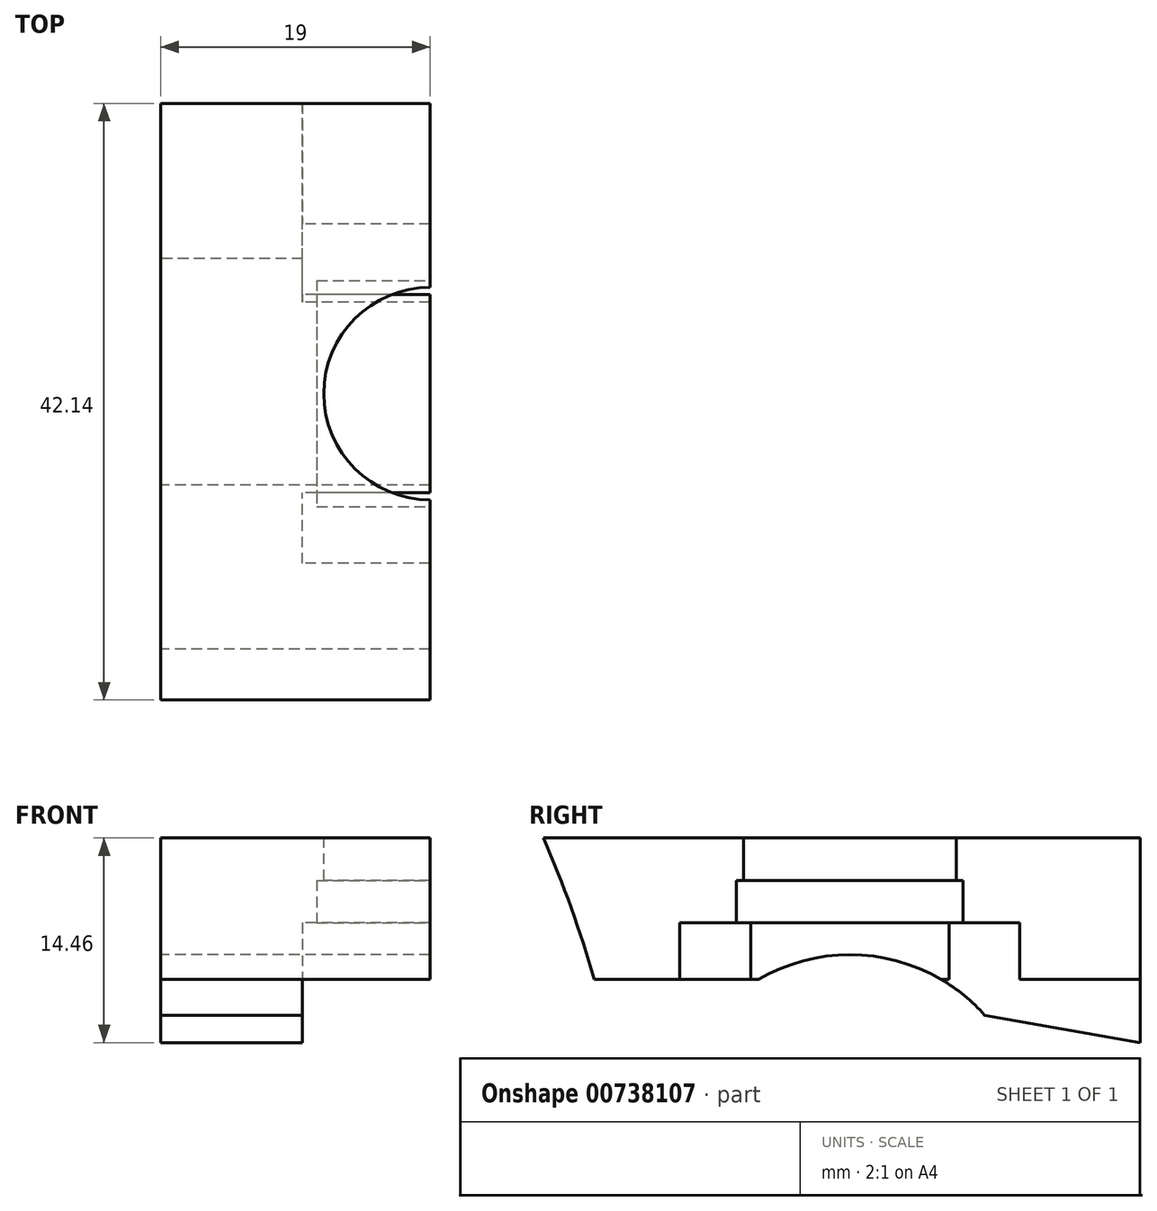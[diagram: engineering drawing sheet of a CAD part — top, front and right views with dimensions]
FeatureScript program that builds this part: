
annotation { "Feature Type Name" : "Feature", "Feature Type Description" : "" }
export const myFeature = defineFeature(function(context is Context, id is Id, definition is map)
    precondition{}
    {
        {
            var Q0;
            Q0=qCreatedBy(makeId("Right.planeOp"),FACE);
            var sketch = newSketch(context, id + "F0", { "sketchPlane" : qUnion([Q0])});
            skLineSegment(sketch, "E0.bottom", {"start": v(21.65, -4.52) * mm, "end": v(-0.35, -4.52) * mm});
            skLineSegment(sketch, "E0.top", {"start": v(21.65, -14.52) * mm, "end": v(-0.35, -14.52) * mm});
            skLineSegment(sketch, "E0.left", {"start": v(21.65, -4.52) * mm, "end": v(21.65, -14.52) * mm});
            skLineSegment(sketch, "E0.right", {"start": v(-0.35, -4.52) * mm, "end": v(-0.35, -14.52) * mm});
            skSolve(sketch);
        }
        {
            var Q0;
            Q0=makeQuery(id+"F0.imprint","IMPRINT",FACE,{"disambiguationData":[TD([[makeQuery(id+"F0.imprint","IMPRINT",EDGE,{"derivedFrom":sQuery(id+"F0.wireOp",EDGE,"E0.bottom")}),1.0]])]});
            extrude(context, id + "F1", {"entities" : qUnion([Q0]), "depth" : 19 * mm, "offsetDistance" : 25 * mm});
        }
        {
            var Q0;
            Q0=makeQuery(id+"FDOM7TivN4VhnVm_1.boolean.opBoolean","MERGE",FACE,{"derivedFrom":[makeQuery(id+"F1.opExtrude","SWEPT_FACE",FACE,{"disambiguationData":[OSD([sQuery(id+"F0.wireOp",EDGE,"E0.bottom")])]}),makeQuery(id+"FDOM7TivN4VhnVm_1.opExtrude","CAP_FACE",FACE,{"disambiguationData":[OSD([sQuery(id+"F9GzfwsNW7Oczpo_1.wireOp",EDGE,"jp0AWD4a-2oyx-ba6K-arvr-44EEn8cdPX9W"),sQuery(id+"F9GzfwsNW7Oczpo_1.wireOp",EDGE,"fE45tPoF-SBnd-VzeE-5eZE-0BWyOUgTPYKQ.bottom"),sQuery(id+"F9GzfwsNW7Oczpo_1.wireOp",EDGE,"fE45tPoF-SBnd-VzeE-5eZE-0BWyOUgTPYKQ.top"),sQuery(id+"F9GzfwsNW7Oczpo_1.wireOp",EDGE,"fE45tPoF-SBnd-VzeE-5eZE-0BWyOUgTPYKQ.left"),sQuery(id+"F9GzfwsNW7Oczpo_1.wireOp",EDGE,"fE45tPoF-SBnd-VzeE-5eZE-0BWyOUgTPYKQ.right")])],"isStart":true})]});
            var sketch = newSketch(context, id + "F2", { "sketchPlane" : qUnion([Q0])});
            skLineSegment(sketch, "E1.bottom", {"start": v(19, -0.35) * mm, "end": v(0, -0.35) * mm});
            skLineSegment(sketch, "E1.top", {"start": v(19, -19.35) * mm, "end": v(0, -19.35) * mm});
            skLineSegment(sketch, "E1.left", {"start": v(19, -0.35) * mm, "end": v(19, -19.35) * mm});
            skLineSegment(sketch, "E1.right", {"start": v(0, -0.35) * mm, "end": v(0, -19.35) * mm});
            skSolve(sketch);
        }
        {
            var Q0;
            {var subQ0=sQuery(id+"F2.wireOp",EDGE,"KGAb659G-aQRa-flcd-oOIB-gSZ9gIRepCPd.top");Q0=makeQuery(id+"F2.imprint","IMPRINT",FACE,{"disambiguationData":[TD([[makeQuery(id+"F2.imprint","IMPRINT",EDGE,{"derivedFrom":subQ0}),-1.0]])]});}
            var Q1;
            Q1=makeQuery(id+"F2.imprint","IMPRINT",FACE,{"disambiguationData":[TD([[makeQuery(id+"F2.imprint","IMPRINT",EDGE,{"derivedFrom":sQuery(id+"F2.wireOp",EDGE,"E1.bottom")}),1.0]])]});
            extrude(context, id + "F3", {"entities" : qUnion([Q0, Q1]), "operationType" : NewBodyOperationType.ADD, "depth" : -10 * mm, "offsetDistance" : 25 * mm});
        }
        {
            var Q0;
            Q0=makeQuery(id+"F3.boolean.opBoolean","MERGE",FACE,{"derivedFrom":[makeQuery(id+"F1.opExtrude","SWEPT_FACE",FACE,{"disambiguationData":[OSD([sQuery(id+"F0.wireOp",EDGE,"E0.top")])]}),makeQuery(id+"F3.opExtrude","CAP_FACE",FACE,{"disambiguationData":[OSD([sQuery(id+"F0.wireOp",EDGE,"E0.bottom"),sQuery(id+"F0.wireOp",EDGE,"E0.right"),sQuery(id+"F2.wireOp",EDGE,"KGAb659G-aQRa-flcd-oOIB-gSZ9gIRepCPd.top"),sQuery(id+"F2.wireOp",EDGE,"KGAb659G-aQRa-flcd-oOIB-gSZ9gIRepCPd.left"),sQuery(id+"F2.wireOp",EDGE,"KGAb659G-aQRa-flcd-oOIB-gSZ9gIRepCPd.right")])],"isStart":false})]});
            var sketch = newSketch(context, id + "F4", { "sketchPlane" : qUnion([Q0])});
            skLineSegment(sketch, "E2.bottom", {"start": v(19, 10.85) * mm, "end": v(10, 10.85) * mm});
            skLineSegment(sketch, "E2.top", {"start": v(19, 5.85) * mm, "end": v(10, 5.85) * mm});
            skLineSegment(sketch, "E2.left", {"start": v(19, 10.85) * mm, "end": v(19, 5.85) * mm});
            skLineSegment(sketch, "E2.right", {"start": v(10, 10.85) * mm, "end": v(10, 5.85) * mm});
            skLineSegment(sketch, "E3.bottom", {"start": v(19, -8.15) * mm, "end": v(10, -8.15) * mm});
            skLineSegment(sketch, "E3.top", {"start": v(19, -13.15) * mm, "end": v(10, -13.15) * mm});
            skLineSegment(sketch, "E3.left", {"start": v(19, -8.15) * mm, "end": v(19, -13.15) * mm});
            skLineSegment(sketch, "E3.right", {"start": v(10, -8.15) * mm, "end": v(10, -13.15) * mm});
            skSolve(sketch);
        }
        {
            var Q0;
            Q0=makeQuery(id+"F4.imprint","IMPRINT",FACE,{"disambiguationData":[TD([[makeQuery(id+"F4.imprint","IMPRINT",EDGE,{"derivedFrom":sQuery(id+"F4.wireOp",EDGE,"E2.bottom")}),1.0]])]});
            var Q1;
            Q1=makeQuery(id+"F4.imprint","IMPRINT",FACE,{"disambiguationData":[TD([[makeQuery(id+"F4.imprint","IMPRINT",EDGE,{"derivedFrom":sQuery(id+"F4.wireOp",EDGE,"E3.bottom")}),1.0]])]});
            extrude(context, id + "F5", {"entities" : qUnion([Q0, Q1]), "operationType" : NewBodyOperationType.REMOVE, "oppositeDirection" : true, "depth" : 4 * mm, "offsetDistance" : 25 * mm});
        }
        {
            var Q0;
            Q0=makeQuery(id+"FUgPAqSj8QWcWe1_1.boolean.opBoolean","MERGE",FACE,{"derivedFrom":[makeQuery(id+"F3.boolean.opBoolean","MERGE",FACE,{"derivedFrom":[makeQuery(id+"F1.opExtrude","CAP_FACE",FACE,{"disambiguationData":[OSD([sQuery(id+"F0.wireOp",EDGE,"E0.bottom"),sQuery(id+"F0.wireOp",EDGE,"E0.top"),sQuery(id+"F0.wireOp",EDGE,"E0.left"),sQuery(id+"F0.wireOp",EDGE,"E0.right")])],"isStart":true}),makeQuery(id+"F3.opExtrude","SWEPT_FACE",FACE,{"disambiguationData":[OSD([sQuery(id+"F2.wireOp",EDGE,"KGAb659G-aQRa-flcd-oOIB-gSZ9gIRepCPd.right")])]})]}),makeQuery(id+"FUgPAqSj8QWcWe1_1.opExtrude","CAP_FACE",FACE,{"disambiguationData":[OSD([sQuery(id+"FlxkZ7T8h6OSLc4_1.wireOp",EDGE,"77buW21n-e5By-ACV8-8WsG-W02AWZP6orzJ.bottom"),sQuery(id+"FlxkZ7T8h6OSLc4_1.wireOp",EDGE,"77buW21n-e5By-ACV8-8WsG-W02AWZP6orzJ.left"),sQuery(id+"FlxkZ7T8h6OSLc4_1.wireOp",EDGE,"Jz0pggAZ-Q1DN-qMmN-crLa-bxhjeAWmcMlq")])],"isStart":false})]});
            var sketch = newSketch(context, id + "F6", { "sketchPlane" : qUnion([Q0])});
            skCircle(sketch, "E4", {"center": v(-1.15, -25.52) * mm, "radius": 12.75 * mm});
            skSolve(sketch);
        }
        {
            var Q0;
            {var subQ0=sQuery(id+"F6.wireOp",EDGE,"E4");var subQ1=makeQuery(id+"F3.boolean.opBoolean","MERGE",EDGE,{"derivedFrom":[makeQuery(id+"F1.opExtrude","CAP_EDGE",EDGE,{"disambiguationData":[OSD([sQuery(id+"F0.wireOp",EDGE,"E0.top")])],"isStart":true}),makeQuery(id+"F3.opExtrude","CAP_EDGE",EDGE,{"disambiguationData":[OSD([sQuery(id+"F2.wireOp",EDGE,"KGAb659G-aQRa-flcd-oOIB-gSZ9gIRepCPd.right")])],"isStart":false})]});var subQ2=makeQuery(id+"F6.imprint","INTERSECT",VERTEX,{"disambiguationData":[OD(0.0)],"derivedFrom":[subQ1,subQ0]});Q0=makeQuery(id+"F6.imprint","IMPRINT",FACE,{"disambiguationData":[TD([[makeQuery(id+"F6.imprint","IMPRINT",EDGE,{"disambiguationData":[TD([[subQ2,1.0]])],"derivedFrom":subQ0}),1.0]])]});}
            var Q1;
            {var subQ0=sQuery(id+"F6.wireOp",EDGE,"E4");var subQ1=makeQuery(id+"F3.boolean.opBoolean","MERGE",EDGE,{"derivedFrom":[makeQuery(id+"F1.opExtrude","CAP_EDGE",EDGE,{"disambiguationData":[OSD([sQuery(id+"F0.wireOp",EDGE,"E0.top")])],"isStart":true}),makeQuery(id+"F3.opExtrude","CAP_EDGE",EDGE,{"disambiguationData":[OSD([sQuery(id+"F2.wireOp",EDGE,"KGAb659G-aQRa-flcd-oOIB-gSZ9gIRepCPd.right")])],"isStart":false})]});var subQ2=makeQuery(id+"F6.imprint","INTERSECT",VERTEX,{"disambiguationData":[OD(0.0)],"derivedFrom":[subQ1,subQ0]});Q1=makeQuery(id+"F6.imprint","IMPRINT",FACE,{"disambiguationData":[TD([[makeQuery(id+"F6.imprint","IMPRINT",EDGE,{"disambiguationData":[TD([[subQ2,-1.0]])],"derivedFrom":subQ0}),1.0]])]});}
            extrude(context, id + "F7", {"entities" : qUnion([Q0, Q1]), "operationType" : NewBodyOperationType.REMOVE, "oppositeDirection" : true, "depth" : 25 * mm, "offsetDistance" : 25 * mm});
        }
        {
            var Q0;
            Q0=makeQuery(id+"FUgPAqSj8QWcWe1_1.boolean.opBoolean","MERGE",FACE,{"derivedFrom":[makeQuery(id+"F3.boolean.opBoolean","MERGE",FACE,{"derivedFrom":[makeQuery(id+"F1.opExtrude","CAP_FACE",FACE,{"disambiguationData":[OSD([sQuery(id+"F0.wireOp",EDGE,"E0.bottom"),sQuery(id+"F0.wireOp",EDGE,"E0.top"),sQuery(id+"F0.wireOp",EDGE,"E0.left"),sQuery(id+"F0.wireOp",EDGE,"E0.right")])],"isStart":true}),makeQuery(id+"F3.opExtrude","SWEPT_FACE",FACE,{"disambiguationData":[OSD([sQuery(id+"F2.wireOp",EDGE,"KGAb659G-aQRa-flcd-oOIB-gSZ9gIRepCPd.right")])]})]}),makeQuery(id+"FUgPAqSj8QWcWe1_1.opExtrude","CAP_FACE",FACE,{"disambiguationData":[OSD([sQuery(id+"FlxkZ7T8h6OSLc4_1.wireOp",EDGE,"77buW21n-e5By-ACV8-8WsG-W02AWZP6orzJ.bottom"),sQuery(id+"FlxkZ7T8h6OSLc4_1.wireOp",EDGE,"77buW21n-e5By-ACV8-8WsG-W02AWZP6orzJ.left"),sQuery(id+"FlxkZ7T8h6OSLc4_1.wireOp",EDGE,"Jz0pggAZ-Q1DN-qMmN-crLa-bxhjeAWmcMlq")])],"isStart":false})]});
            var sketch = newSketch(context, id + "F8", { "sketchPlane" : qUnion([Q0])});
            skCircle(sketch, "E5", {"center": v(93.81, -36.52) * mm, "radius": 80 * mm});
            skLineSegment(sketch, "E6.bottom", {"start": v(19.35, -4.52) * mm, "end": v(33.13, -4.52) * mm});
            skLineSegment(sketch, "E6.top", {"start": v(19.35, -14.52) * mm, "end": v(33.13, -14.52) * mm});
            skLineSegment(sketch, "E6.left", {"start": v(19.35, -4.52) * mm, "end": v(19.35, -14.52) * mm});
            skLineSegment(sketch, "E6.right", {"start": v(33.13, -4.52) * mm, "end": v(33.13, -14.52) * mm});
            skSolve(sketch);
        }
        {
            var Q0;
            {var subQ2=sQuery(id+"F2.wireOp",EDGE,"KGAb659G-aQRa-flcd-oOIB-gSZ9gIRepCPd.right");var subQ6=sQuery(id+"F2.wireOp",EDGE,"KGAb659G-aQRa-flcd-oOIB-gSZ9gIRepCPd.top");var subQ11=makeQuery(id+"F3.opExtrude","SWEPT_EDGE",EDGE,{"disambiguationData":[OSD([subQ6,subQ2])]});Q0=makeQuery(id+"F8.imprint","IMPRINT",FACE,{"disambiguationData":[TD([[makeQuery(id+"F8.imprint","IMPRINT",EDGE,{"derivedFrom":subQ11}),1.0]])]});}
            var Q1;
            {var subQ5=sQuery(id+"F8.wireOp",EDGE,"E6.left");Q1=makeQuery(id+"F8.imprint","IMPRINT",FACE,{"disambiguationData":[TD([[makeQuery(id+"F8.imprint","IMPRINT",EDGE,{"derivedFrom":subQ5}),-1.0]])]});}
            extrude(context, id + "F9", {"entities" : qUnion([Q0, Q1]), "operationType" : NewBodyOperationType.ADD, "oppositeDirection" : true, "depth" : 19 * mm, "offsetDistance" : 25 * mm});
        }
        {
            var Q0;
            {var subQ0=sQuery(id+"F8.wireOp",EDGE,"E6.left");var subQ1=sQuery(id+"F8.wireOp",EDGE,"E5");var subQ2=makeQuery(id+"F8.imprint","INTERSECT",VERTEX,{"derivedFrom":[subQ1,subQ0]});Q0=makeQuery(id+"F8.imprint","IMPRINT",FACE,{"disambiguationData":[TD([[makeQuery(id+"F8.imprint","IMPRINT",EDGE,{"disambiguationData":[TD([[subQ2,-1.0]])],"derivedFrom":subQ1}),1.0]])]});}
            extrude(context, id + "F10", {"entities" : qUnion([Q0]), "operationType" : NewBodyOperationType.REMOVE, "oppositeDirection" : true, "depth" : 25 * mm, "offsetDistance" : 25 * mm});
        }
        {
            var Q0;
            Q0=makeQuery(id+"F9.boolean.opBoolean","MERGE",FACE,{"derivedFrom":[makeQuery(id+"F3.boolean.opBoolean","MERGE",FACE,{"derivedFrom":[makeQuery(id+"F1.opExtrude","CAP_FACE",FACE,{"disambiguationData":[OSD([sQuery(id+"F0.wireOp",EDGE,"E0.bottom"),sQuery(id+"F0.wireOp",EDGE,"E0.top"),sQuery(id+"F0.wireOp",EDGE,"E0.left"),sQuery(id+"F0.wireOp",EDGE,"E0.right")])],"isStart":true}),makeQuery(id+"F3.opExtrude","SWEPT_FACE",FACE,{"disambiguationData":[OSD([sQuery(id+"F2.wireOp",EDGE,"KGAb659G-aQRa-flcd-oOIB-gSZ9gIRepCPd.right")])]})]}),makeQuery(id+"F9.opExtrude","CAP_FACE",FACE,{"disambiguationData":[OSD([sQuery(id+"F8.wireOp",EDGE,"E5"),sQuery(id+"F8.wireOp",EDGE,"E6.bottom"),sQuery(id+"F8.wireOp",EDGE,"E6.left")])],"isStart":true})]});
            var sketch = newSketch(context, id + "F11", { "sketchPlane" : qUnion([Q0])});
            skCircle(sketch, "E7", {"center": v(-1.15, -25.52) * mm, "radius": 12.75 * mm});
            skCircle(sketch, "E8", {"center": v(-1.15, -25.52) * mm, "radius": 10 * mm});
            skLineSegment(sketch, "E9", {"start": v(-1.15, -25.52) * mm, "end": v(-29.86, -30.58) * mm});
            skLineSegment(sketch, "E10", {"start": v(-1.15, -25.52) * mm, "end": v(-11.15, -25.52) * mm});
            skLineSegment(sketch, "E11", {"start": v(-29.86, -30.58) * mm, "end": v(-31.6, -20.74) * mm});
            skLineSegment(sketch, "E12", {"start": v(-1.15, -25.52) * mm, "end": v(-2.89, -15.67) * mm});
            skLineSegment(sketch, "E13", {"start": v(-2.89, -15.67) * mm, "end": v(-31.6, -20.74) * mm});
            skLineSegment(sketch, "E14", {"start": v(-21.65, -14.52) * mm, "end": v(-21.65, -18.98) * mm});
            skLineSegment(sketch, "E15", {"start": v(-21.65, -4.52) * mm, "end": v(-21.65, -14.52) * mm});
            skSolve(sketch);
        }
        {
            var Q0;
            {var subQ9=sQuery(id+"F11.wireOp",EDGE,"E14");Q0=makeQuery(id+"F11.imprint","IMPRINT",FACE,{"disambiguationData":[TD([[makeQuery(id+"F11.imprint","IMPRINT",EDGE,{"derivedFrom":subQ9}),1.0]])]});}
            extrude(context, id + "F12", {"entities" : qUnion([Q0]), "operationType" : NewBodyOperationType.ADD, "depth" : -10 * mm, "offsetDistance" : 25 * mm});
        }
        {
            var Q0;
            Q0=makeQuery(id+"F9.boolean.opBoolean","MERGE",FACE,{"derivedFrom":[makeQuery(id+"F3.boolean.opBoolean","MERGE",FACE,{"derivedFrom":[makeQuery(id+"F1.opExtrude","CAP_FACE",FACE,{"disambiguationData":[OSD([sQuery(id+"F0.wireOp",EDGE,"E0.bottom"),sQuery(id+"F0.wireOp",EDGE,"E0.top"),sQuery(id+"F0.wireOp",EDGE,"E0.left"),sQuery(id+"F0.wireOp",EDGE,"E0.right")])],"isStart":false}),makeQuery(id+"F3.opExtrude","SWEPT_FACE",FACE,{"disambiguationData":[OSD([sQuery(id+"F2.wireOp",EDGE,"E1.left")])]})]}),makeQuery(id+"F9.opExtrude","CAP_FACE",FACE,{"disambiguationData":[OSD([sQuery(id+"F8.wireOp",EDGE,"E5"),sQuery(id+"F8.wireOp",EDGE,"E6.bottom"),sQuery(id+"F8.wireOp",EDGE,"E6.left")])],"isStart":false})]});
            var sketch = newSketch(context, id + "F13", { "sketchPlane" : qUnion([Q0])});
            skLineSegment(sketch, "E16.bottom", {"start": v(-6.85, -4.52) * mm, "end": v(9.15, -4.52) * mm});
            skLineSegment(sketch, "E16.top", {"start": v(-6.85, -10.52) * mm, "end": v(9.15, -10.52) * mm});
            skLineSegment(sketch, "E16.left", {"start": v(-6.85, -4.52) * mm, "end": v(-6.85, -10.52) * mm});
            skLineSegment(sketch, "E16.right", {"start": v(9.15, -4.52) * mm, "end": v(9.15, -10.52) * mm});
            skLineSegment(sketch, "E17", {"start": v(1.15, -4.52) * mm, "end": v(1.15, -10.52) * mm});
            skLineSegment(sketch, "E18", {"start": v(21.65, -4.52) * mm, "end": v(21.65, -14.52) * mm});
            skSolve(sketch);
        }
        {
            var Q0;
            {var subQ4=sQuery(id+"F13.wireOp",EDGE,"E16.left");Q0=makeQuery(id+"F13.imprint","IMPRINT",FACE,{"disambiguationData":[TD([[makeQuery(id+"F13.imprint","IMPRINT",EDGE,{"derivedFrom":subQ4}),1.0]])]});}
            var Q1;
            {var subQ0=sQuery(id+"F13.wireOp",EDGE,"E16.right");Q1=makeQuery(id+"F13.imprint","IMPRINT",FACE,{"disambiguationData":[TD([[makeQuery(id+"F13.imprint","IMPRINT",EDGE,{"derivedFrom":subQ0}),-1.0]])]});}
            extrude(context, id + "F14", {"entities" : qUnion([Q0, Q1]), "operationType" : NewBodyOperationType.REMOVE, "oppositeDirection" : true, "depth" : 8 * mm, "offsetDistance" : 25 * mm});
        }
        {
            var Q0;
            Q0=makeQuery(id+"F9.boolean.opBoolean","MERGE",FACE,{"derivedFrom":[makeQuery(id+"F3.boolean.opBoolean","MERGE",FACE,{"derivedFrom":[makeQuery(id+"F1.opExtrude","SWEPT_FACE",FACE,{"disambiguationData":[OSD([sQuery(id+"F0.wireOp",EDGE,"E0.bottom")])]}),makeQuery(id+"F3.opExtrude","CAP_FACE",FACE,{"disambiguationData":[OSD([sQuery(id+"F2.wireOp",EDGE,"E1.bottom"),sQuery(id+"F2.wireOp",EDGE,"E1.top"),sQuery(id+"F2.wireOp",EDGE,"E1.left"),sQuery(id+"F2.wireOp",EDGE,"E1.right")])],"isStart":true})]}),makeQuery(id+"F9.opExtrude","SWEPT_FACE",FACE,{"disambiguationData":[OSD([sQuery(id+"F8.wireOp",EDGE,"E6.bottom")])]})]});
            var sketch = newSketch(context, id + "F15", { "sketchPlane" : qUnion([Q0])});
            skCircle(sketch, "E19", {"center": v(19, 1.15) * mm, "radius": 7.5 * mm});
            skPoint(sketch, "E19.centerSnap0", {"position": v(11, 1.15) * mm});
            skLineSegment(sketch, "E20.bottom", {"start": v(19, 9.15) * mm, "end": v(11, 9.15) * mm});
            skLineSegment(sketch, "E20.top", {"start": v(19, -6.85) * mm, "end": v(11, -6.85) * mm});
            skLineSegment(sketch, "E20.left", {"start": v(19, 9.15) * mm, "end": v(19, -6.85) * mm});
            skLineSegment(sketch, "E20.right", {"start": v(11, 9.15) * mm, "end": v(11, -6.85) * mm});
            skSolve(sketch);
        }
        {
            var Q0;
            {var subQ1=sQuery(id+"F15.wireOp",EDGE,"E20.bottom");Q0=makeQuery(id+"F15.imprint","IMPRINT",FACE,{"disambiguationData":[TD([[makeQuery(id+"F15.imprint","IMPRINT",EDGE,{"derivedFrom":subQ1}),-1.0]])]});}
            extrude(context, id + "F16", {"entities" : qUnion([Q0]), "operationType" : NewBodyOperationType.ADD, "depth" : -3 * mm, "offsetDistance" : 25 * mm});
        }
    });
